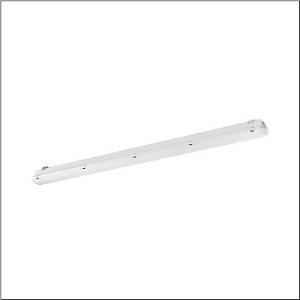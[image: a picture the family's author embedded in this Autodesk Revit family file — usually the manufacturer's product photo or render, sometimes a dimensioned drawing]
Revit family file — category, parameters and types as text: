
# Revit family: monsun_r__11xtreme_mo_51fe107p460j_10b9
name_source: partatom
category: Lighting Fixtures
units: mm (PartAtom-declared; Revit-internal decimal feet)

## family parameters
Cut with Voids When Loaded = No
Host = Face
Light Source = No
Part Type = Normal
Room Calculation Point = No
Round Connector Dimension = Use Diameter
Shared = No

## types (1)
- Monsun® 11Xtreme MO (1 x LED, 6370 lm, 34.9 W, 4000K)
    Apparent Load = 35 VA
    CIE Flux Codes = 47 77 93 94 100
    Color Rendering = 80
    Color Temperature = 4000K
    Default Elevation = 1800 mm
    Description = Monsun® 11Xtreme MO, damp-proof luminaire, chain hanger, primary optical cover: enclosure, of PMMA, light emission: direct distribution, primary light characteristic: symmetric, installation type: suspended mounting, surface-mounted, horizontal mounting, vertical mounting, LED, rated luminous flux: 6.370lm, luminous efficacy: 175lm/W, light colour: 840, colour temperature: 4000K, control gear: ON/OFF, with terminal, 3-pole, max. 2.5mm², mains connection: 220..240V, AC, 50/60Hz, rated input power: 37W, luminaire housing, of glass-fibre reinforced polyester, uncoated, bright grey, incl. chain hanger, length: 1.590mm, width: 90mm, height: 88mm, clip for enclosure, of stainless steel (V2A), ceiling mounting element, of stainless steel (V2A), chain hanger, of stainless steel (V2A), protection rating (complete): IP66, insulation class (complete): insulation class I (protective earthing), certification: CE, ENEC, VDE, UKCA, protection symbol: D, impact resistance: IK04, permissible operating ambient temperature: -35..+55°C, standard: EN 50419, EN 60598-2-1, corresponds to IFS (International Featured Standards) requirements for safety and quality in the food industry, for indoor or canopied outdoor use, no direct snow, no direct sun, no direct rain, contact your sales advisor before using the luminaires in applications with unclear chemical exposure, large temperature fluctuations or condensation-forming humidity, LABS conformity tested according to VDMA 24364:2018-05, packaging unit: 1 piece
    Height = 88 mm
    Lamp = 1 x LED
    Lamp Light Flux = 6370 lm
    Lamp Power = 34.9 W
    Lamp count = 1
    Length = 1590 mm
    Luminous efficacy = 183 lm/W
    Manufacturer = Siteco
    ModVariant = No
    Model = 51FE107P460J
    Mounting Place = Ceiling
    Mounting Type = Surface mounted
    Number of Poles = 1
    OnlyDefault = Yes
    Power Factor = 1
    Product Name = Monsun® 11Xtreme MO
    Product group = damp-proof luminaire
    ProductGroupID = 300
    Protection Class = Protection class I
    Protection Degree = IP 66
    RLX_Detail_Level = 1
    RLX_Emergency_Light_Flux = 0 lm
    RLX_Emergency_Type = 0
    RLX_Emergency_Type_DB = No
    RlxData = <blob elided: 12397 chars, md5=1f3a6a02>
    Socket = socket
    Standby Power = 0 W
    System Light Flux = 6370 lm
    System Power = 35 W
    Type Comments = Product without accessories
    Type Image = l_1349234.jpg
    URL = http://relux.com
    VarID = ---
    Voltage = 0 V
    Weight = 0.00 kg
    Width = 90 mm

## geometry (parser evidence)
native form markers: Sweep x10
no freeform markers — native parametric forms only
